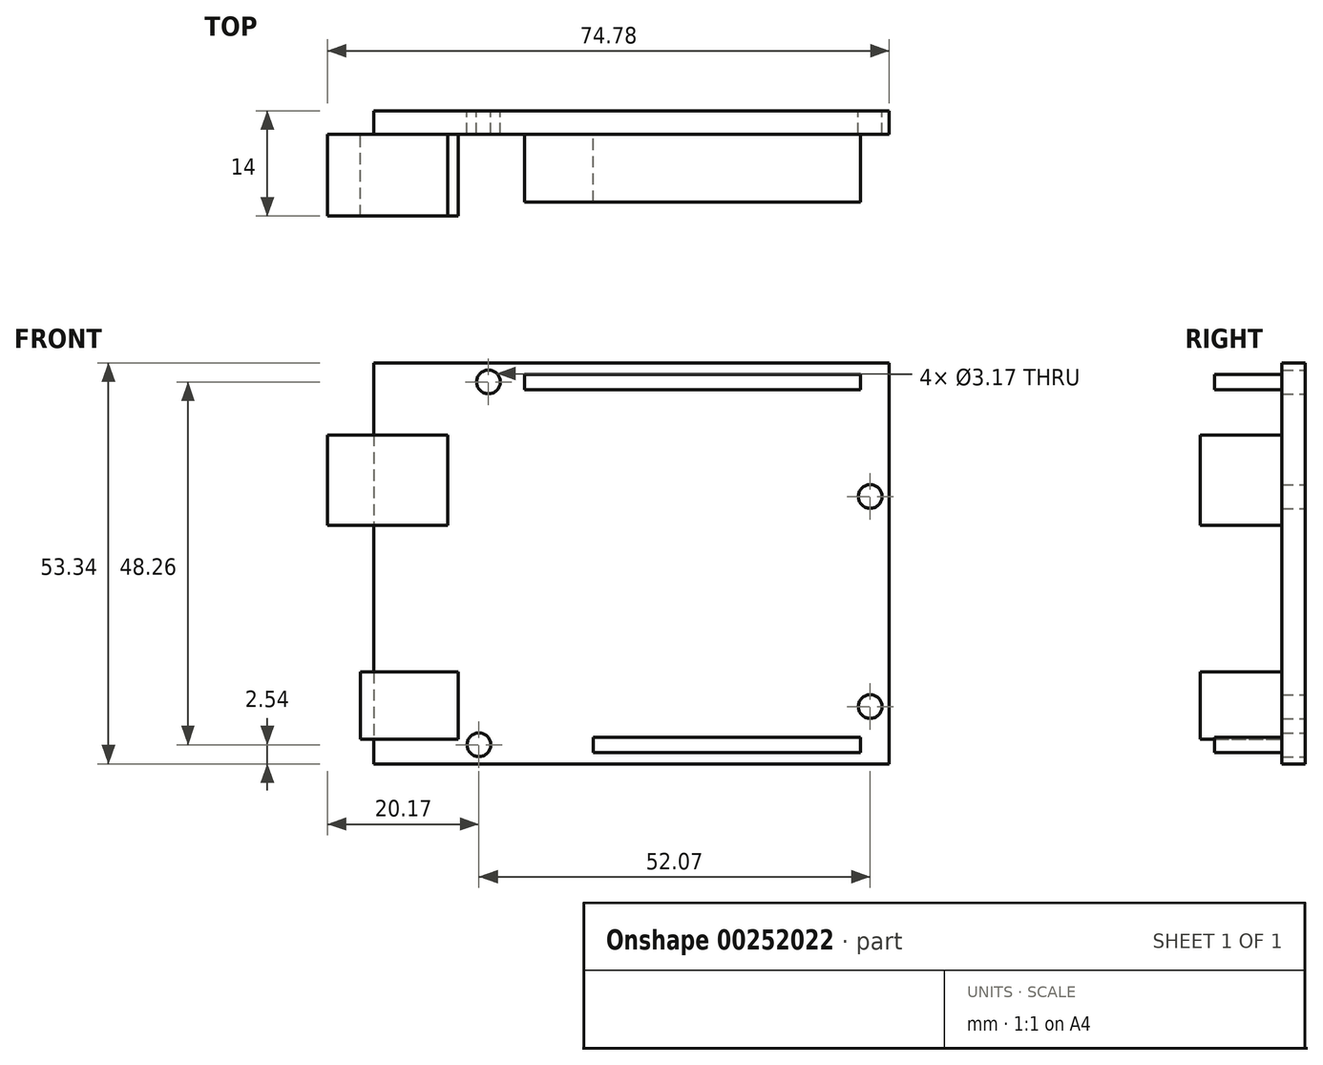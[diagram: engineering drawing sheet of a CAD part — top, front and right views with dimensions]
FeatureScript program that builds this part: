
annotation { "Feature Type Name" : "Feature", "Feature Type Description" : "" }
export const myFeature = defineFeature(function(context is Context, id is Id, definition is map)
    precondition{}
    {
        {
            var Q0;
            Q0=qCreatedBy(makeId("Front.planeOp"),FACE);
            var sketch = newSketch(context, id + "F0", { "sketchPlane" : qUnion([Q0])});
            skLineSegment(sketch, "E0.bottom", {"start": v(0, 53.34) * mm, "end": v(68.58, 53.34) * mm});
            skLineSegment(sketch, "E0.top", {"start": v(0, 0) * mm, "end": v(68.58, 0) * mm});
            skLineSegment(sketch, "E0.left", {"start": v(0, 53.34) * mm, "end": v(0, 0) * mm});
            skLineSegment(sketch, "E0.right", {"start": v(68.58, 53.34) * mm, "end": v(68.58, 0) * mm});
            skCircle(sketch, "E1", {"center": v(13.97, 2.54) * mm, "radius": 1.59 * mm});
            skCircle(sketch, "E2", {"center": v(66.04, 7.62) * mm, "radius": 1.59 * mm});
            skCircle(sketch, "E3", {"center": v(66.04, 35.56) * mm, "radius": 1.59 * mm});
            skCircle(sketch, "E4", {"center": v(15.24, 50.8) * mm, "radius": 1.59 * mm});
            skSolve(sketch);
        }
        {
            var Q0;
            Q0=makeQuery(id+"F0.imprint","IMPRINT",FACE,{"disambiguationData":[TD([[makeQuery(id+"F0.imprint","IMPRINT",EDGE,{"derivedFrom":sQuery(id+"F0.wireOp",EDGE,"E0.bottom")}),-1.0]])]});
            extrude(context, id + "F1", {"entities" : qUnion([Q0]), "depth" : 3.1 * mm});
        }
        {
            var Q0;
            Q0=makeQuery(id+"F1.opExtrude","CAP_FACE",FACE,{"disambiguationData":[OSD([sQuery(id+"F0.wireOp",EDGE,"E0.bottom"),sQuery(id+"F0.wireOp",EDGE,"E0.top"),sQuery(id+"F0.wireOp",EDGE,"E0.left"),sQuery(id+"F0.wireOp",EDGE,"E0.right"),sQuery(id+"F0.wireOp",EDGE,"E1"),sQuery(id+"F0.wireOp",EDGE,"E2"),sQuery(id+"F0.wireOp",EDGE,"E3"),sQuery(id+"F0.wireOp",EDGE,"E4")])],"isStart":false});
            var sketch = newSketch(context, id + "F2", { "sketchPlane" : qUnion([Q0])});
            skLineSegment(sketch, "E5.bottom", {"start": v(-6.2, 43.74) * mm, "end": v(9.8, 43.74) * mm});
            skLineSegment(sketch, "E5.top", {"start": v(-6.2, 31.74) * mm, "end": v(9.8, 31.74) * mm});
            skLineSegment(sketch, "E5.left", {"start": v(-6.2, 43.74) * mm, "end": v(-6.2, 31.74) * mm});
            skLineSegment(sketch, "E5.right", {"start": v(9.8, 43.74) * mm, "end": v(9.8, 31.74) * mm});
            skLineSegment(sketch, "E6.bottom", {"start": v(-1.8, 12.2) * mm, "end": v(11.2, 12.2) * mm});
            skLineSegment(sketch, "E6.top", {"start": v(-1.8, 3.3) * mm, "end": v(11.2, 3.3) * mm});
            skLineSegment(sketch, "E6.left", {"start": v(-1.8, 12.2) * mm, "end": v(-1.8, 3.3) * mm});
            skLineSegment(sketch, "E6.right", {"start": v(11.2, 12.2) * mm, "end": v(11.2, 3.3) * mm});
            skSolve(sketch);
        }
        {
            var Q0;
            {var subQ0=sQuery(id+"F2.wireOp",EDGE,"E5.left");Q0=makeQuery(id+"F2.imprint","IMPRINT",FACE,{"disambiguationData":[TD([[makeQuery(id+"F2.imprint","IMPRINT",EDGE,{"derivedFrom":subQ0}),1.0]])]});}
            var Q1;
            {var subQ0=sQuery(id+"F2.wireOp",EDGE,"E5.right");Q1=makeQuery(id+"F2.imprint","IMPRINT",FACE,{"disambiguationData":[TD([[makeQuery(id+"F2.imprint","IMPRINT",EDGE,{"derivedFrom":subQ0}),-1.0]])]});}
            var Q2;
            {var subQ0=sQuery(id+"F2.wireOp",EDGE,"E6.right");Q2=makeQuery(id+"F2.imprint","IMPRINT",FACE,{"disambiguationData":[TD([[makeQuery(id+"F2.imprint","IMPRINT",EDGE,{"derivedFrom":subQ0}),-1.0]])]});}
            var Q3;
            {var subQ0=sQuery(id+"F2.wireOp",EDGE,"E6.left");Q3=makeQuery(id+"F2.imprint","IMPRINT",FACE,{"disambiguationData":[TD([[makeQuery(id+"F2.imprint","IMPRINT",EDGE,{"derivedFrom":subQ0}),1.0]])]});}
            extrude(context, id + "F3", {"entities" : qUnion([Q0, Q1, Q2, Q3]), "operationType" : NewBodyOperationType.ADD, "depth" : 10.9 * mm});
        }
        {
            var Q0;
            Q0=makeQuery(id+"F1.opExtrude","CAP_FACE",FACE,{"disambiguationData":[OSD([sQuery(id+"F0.wireOp",EDGE,"E0.bottom"),sQuery(id+"F0.wireOp",EDGE,"E0.top"),sQuery(id+"F0.wireOp",EDGE,"E0.left"),sQuery(id+"F0.wireOp",EDGE,"E0.right"),sQuery(id+"F0.wireOp",EDGE,"E1"),sQuery(id+"F0.wireOp",EDGE,"E2"),sQuery(id+"F0.wireOp",EDGE,"E3"),sQuery(id+"F0.wireOp",EDGE,"E4")])],"isStart":false});
            var sketch = newSketch(context, id + "F4", { "sketchPlane" : qUnion([Q0])});
            skLineSegment(sketch, "E7.bottom", {"start": v(20.07, 51.82) * mm, "end": v(64.77, 51.82) * mm});
            skLineSegment(sketch, "E7.top", {"start": v(20.07, 49.78) * mm, "end": v(64.77, 49.78) * mm});
            skLineSegment(sketch, "E7.left", {"start": v(20.07, 51.82) * mm, "end": v(20.07, 49.78) * mm});
            skLineSegment(sketch, "E7.right", {"start": v(64.77, 51.82) * mm, "end": v(64.77, 49.78) * mm});
            skLineSegment(sketch, "E8.bottom", {"start": v(29.21, 3.56) * mm, "end": v(64.77, 3.56) * mm});
            skLineSegment(sketch, "E8.top", {"start": v(29.21, 1.52) * mm, "end": v(64.77, 1.52) * mm});
            skLineSegment(sketch, "E8.left", {"start": v(29.21, 3.56) * mm, "end": v(29.21, 1.52) * mm});
            skLineSegment(sketch, "E8.right", {"start": v(64.77, 3.56) * mm, "end": v(64.77, 1.52) * mm});
            skSolve(sketch);
        }
        {
            var Q0;
            Q0=makeQuery(id+"F4.imprint","IMPRINT",FACE,{"disambiguationData":[TD([[makeQuery(id+"F4.imprint","IMPRINT",EDGE,{"derivedFrom":sQuery(id+"F4.wireOp",EDGE,"E7.bottom")}),-1.0]])]});
            var Q1;
            Q1=makeQuery(id+"F4.imprint","IMPRINT",FACE,{"disambiguationData":[TD([[makeQuery(id+"F4.imprint","IMPRINT",EDGE,{"derivedFrom":sQuery(id+"F4.wireOp",EDGE,"E8.bottom")}),-1.0]])]});
            extrude(context, id + "F5", {"entities" : qUnion([Q0, Q1]), "operationType" : NewBodyOperationType.ADD, "depth" : 9 * mm});
        }
    });
